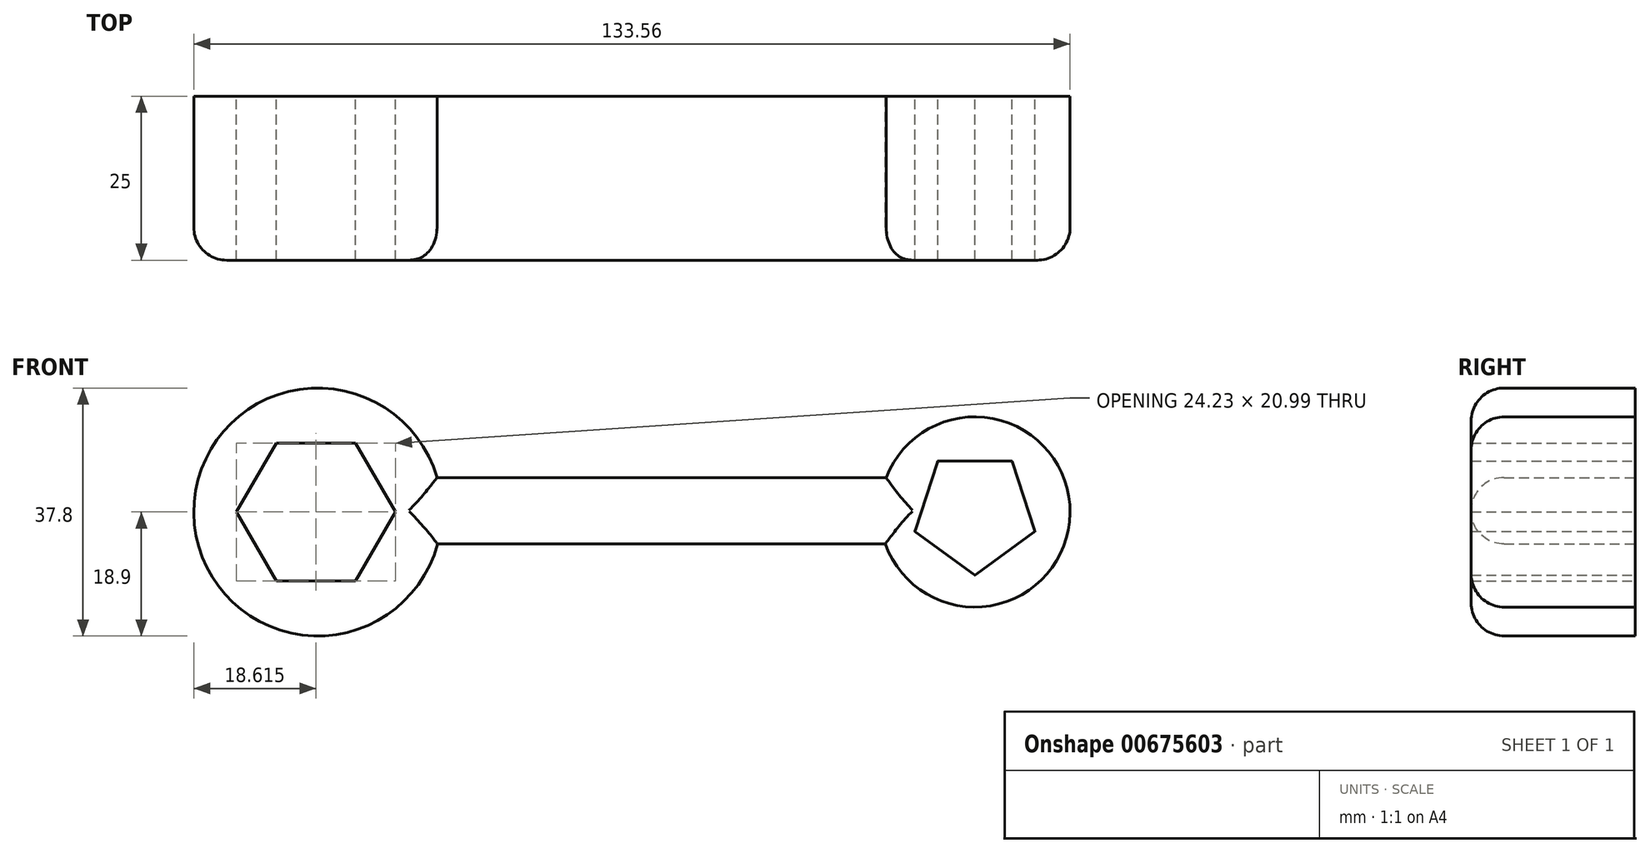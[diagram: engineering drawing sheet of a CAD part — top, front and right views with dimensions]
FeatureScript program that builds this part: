
annotation { "Feature Type Name" : "Feature", "Feature Type Description" : "" }
export const myFeature = defineFeature(function(context is Context, id is Id, definition is map)
    precondition{}
    {
        {
            var Q0;
            Q0=qCreatedBy(makeId("Front.planeOp"),FACE);
            var sketch = newSketch(context, id + "F0", { "sketchPlane" : qUnion([Q0])});
            skLineSegment(sketch, "E0.0", {"start": v(-40.16, 10.5) * mm, "end": v(-28.05, 10.5) * mm});
            skLineSegment(sketch, "E0.1", {"start": v(-28.05, 10.5) * mm, "end": v(-21.99, 0) * mm});
            skLineSegment(sketch, "E0.2", {"start": v(-21.99, 0) * mm, "end": v(-28.05, -10.5) * mm});
            skLineSegment(sketch, "E0.3", {"start": v(-28.05, -10.5) * mm, "end": v(-40.16, -10.5) * mm});
            skLineSegment(sketch, "E0.4", {"start": v(-40.16, -10.5) * mm, "end": v(-46.22, 0) * mm});
            skLineSegment(sketch, "E0.5", {"start": v(-46.22, 0) * mm, "end": v(-40.16, 10.5) * mm});
            skPoint(sketch, "E0.0.midPoint", {"position": v(-34.1, 10.5) * mm});
            skCircle(sketch, "E1", {"center": v(-33.82, 0) * mm, "radius": 18.9 * mm});
            skCircle(sketch, "E2", {"center": v(66.34, 0) * mm, "radius": 14.5 * mm});
            skLineSegment(sketch, "E3", {"start": v(-15.66, 5.25) * mm, "end": v(52.82, 5.25) * mm});
            skPoint(sketch, "E3.startSnap0", {"position": v(-25.02, 5.25) * mm});
            skLineSegment(sketch, "E4", {"start": v(52.68, -4.89) * mm, "end": v(-15.56, -4.89) * mm});
            skLineSegment(sketch, "E5.0.right", {"start": v(-15.66, -4.75) * mm, "end": v(52.82, -4.75) * mm});
            skCircle(sketch, "E6.cCircle", {"center": v(66.34, 0) * mm, "radius": 7.8 * mm, "construction": true});
            skLineSegment(sketch, "E6.0", {"start": v(60.68, 7.8) * mm, "end": v(72, 7.8) * mm});
            skLineSegment(sketch, "E6.1", {"start": v(72, 7.8) * mm, "end": v(75.5, -2.98) * mm});
            skLineSegment(sketch, "E6.2", {"start": v(75.5, -2.98) * mm, "end": v(66.34, -9.63) * mm});
            skLineSegment(sketch, "E6.3", {"start": v(66.34, -9.63) * mm, "end": v(57.18, -2.98) * mm});
            skLineSegment(sketch, "E6.4", {"start": v(57.18, -2.98) * mm, "end": v(60.68, 7.8) * mm});
            skPoint(sketch, "E6.0.midPoint", {"position": v(66.34, 7.8) * mm});
            skSolve(sketch);
        }
        {
            var Q0;
            Q0 = qSketchRegion(id + "F0", true);
            extrude(context, id + "F1", {"entities" : qUnion([Q0]), "depth" : 25 * mm, "offsetDistance" : 25 * mm});
        }
        {
            var Q0;
            Q0=makeQuery(id+"F1.opExtrude","CAP_EDGE",EDGE,{"disambiguationData":[OSD([sQuery(id+"F0.wireOp",EDGE,"E1")])],"isStart":false});
            var Q1;
            Q1=makeQuery(id+"F1.opExtrude","CAP_EDGE",EDGE,{"disambiguationData":[OSD([sQuery(id+"F0.wireOp",EDGE,"E3")])],"isStart":false});
            var Q2;
            Q2=makeQuery(id+"F1.opExtrude","CAP_EDGE",EDGE,{"disambiguationData":[OSD([sQuery(id+"F0.wireOp",EDGE,"E2")])],"isStart":false});
            var Q3;
            Q3=makeQuery(id+"F1.opExtrude","CAP_EDGE",EDGE,{"disambiguationData":[OSD([sQuery(id+"F0.wireOp",EDGE,"E4")])],"isStart":false});
            fillet(context, id + "F2", {"entities" : qUnion([Q0, Q1, Q2, Q3]), "radius" : 5 * mm, "tangentPropagation" : true, "allowEdgeOverflow" : false});
        }
    });
